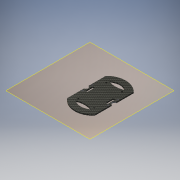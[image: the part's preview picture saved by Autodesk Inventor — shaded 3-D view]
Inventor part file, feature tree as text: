
AUTODESK INVENTOR PART (.ipt)
format: ipt  version: 2017 (Build 210142000, 142)  size: 208,384 bytes
history: native  units: mm
features: other x5, extrude x3, sketch x3, reference x2
ambient origin geometry x8: Origin, YZ Plane, XZ Plane, XY Plane, X Axis, Y Axis, Z Axis, Center Point
bodies: Body1 (feature_tree)
feature tree (13):
  other  "Bryła1"
  other  "Płaszczyzna konstrukcyjna1"
  extrude  "Wyciągnięcie proste1"  Depth=4.0mm
  extrude  "Wyciągnięcie proste2"  Depth=3.5mm
  extrude  "Wyciągnięcie proste3"  Depth=12.5mm
  sketch  "Szkic1"
  reference  "Odniesienie1"
  reference  "Odniesienie2"
  sketch  "Szkic2"
  sketch  "Szkic3"
  other  "Zespół1"
  other  "li-pol:1"
  other  "rama:1"
